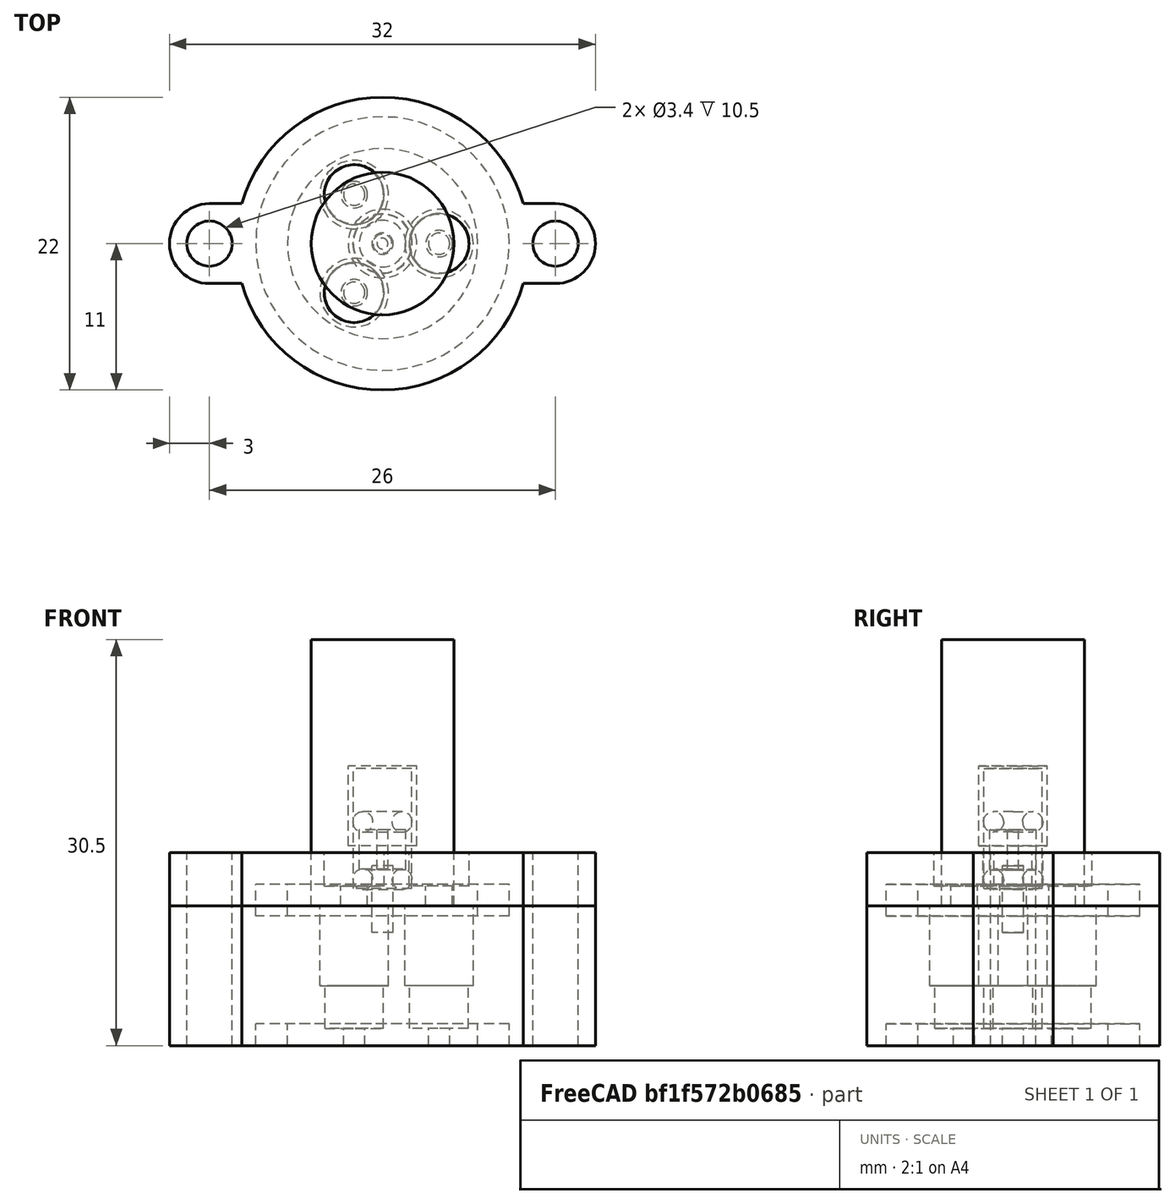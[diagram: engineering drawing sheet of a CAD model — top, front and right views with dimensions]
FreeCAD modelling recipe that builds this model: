
FCSTD DOCUMENT  (FreeCAD 0.17R13509 (Git))
Label: ceramic_wire_feedthroughs
License: All rights reserved
LicenseURL: http://en.wikipedia.org/wiki/All_rights_reserved
objects: Part::Cylinder×46, Part::MultiFuse×12, Part::Cut×9, Part::Box×8, Part::FeaturePython×4, Part::Feature×2, App::FeaturePython×1
note: 81 computed .brp shape members not serialized (recipe doc carries the construction recipe); baked Part::Feature solids carry a one-line shape summary decoded from their .brp

FEATURE [Part::Cylinder] Cylinder151  label="WireFeedsMount002"
  Angle = 360
  AttacherType = Attacher::AttachEngine3D
  Height = 11
  Placement = pos=(13,0,0) rot=(0,0,1;0rad)
  Radius = 1.7
FEATURE [Part::Cylinder] Cylinder155  label="Cylinder009"
  Angle = 360
  AttacherType = Attacher::AttachEngine3D
  Height = 2.38125
  Radius = 9.525
  expr: Radius = 3 / 4 * 25.399999999999999 / 2
  expr: Height = 3 / 32 * 25.399999999999999
FEATURE [Part::Cylinder] Cylinder154  label="Cylinder008"
  Angle = 360
  AttacherType = Attacher::AttachEngine3D
  Height = 2.38125
  Radius = 7.14375
  expr: Radius = 9 / 16 * 25.399999999999999 / 2
  expr: Height = 3 / 32 * 25.399999999999999
FEATURE [Part::Feature] Part__Feature001  label="TopOring"
  Placement = pos=(0,0,6.3) rot=(0,0,1;0rad)
  shape: bbox 4.839 x 4.839 x 1.524 mm, 4 faces (baked)
FEATURE [Part::Feature] Part__Feature002  label="BottomOring"
  Placement = pos=(0,0,2) rot=(0,0,1;0rad)
  shape: bbox 4.839 x 4.839 x 1.524 mm, 4 faces (baked)
FEATURE [Part::Cylinder] Cylinder153  label="Body"
  Angle = 360
  AttacherType = Attacher::AttachEngine3D
  Height = 4
  Radius = 11
FEATURE [Part::Cut] Cut019  label="Oring"
  Base = -> Cylinder155
  Placement = pos=(0,0,-0.75) rot=(0,0,1;0rad)
  Tool = -> Cylinder154
FEATURE [Part::Cylinder] Cylinder150  label="WireFeedsMount1"
  Angle = 360
  AttacherType = Attacher::AttachEngine3D
  Height = 11
  Placement = pos=(-13,0,0) rot=(0,0,1;0rad)
  Radius = 1.7
FEATURE [Part::Cylinder] Cylinder147  label="ThreadedSection"
  Angle = 360
  AttacherType = Attacher::AttachEngine3D
  Height = 1
  Placement = pos=(0,0,4.5) rot=(0,0,1;0rad)
  Radius = 1
FEATURE [Part::Cylinder] Cylinder149  label="FTBead"
  Angle = 360
  AttacherType = Attacher::AttachEngine3D
  Height = 3
  Placement = pos=(0,0,2.7) rot=(0,0,1;0rad)
  Radius = 1.75
  expr: Radius = 3.5 / 2
FEATURE [Part::Cylinder] Cylinder152  label="RFFeeds005"
  Angle = 360
  AttacherType = Attacher::AttachEngine3D
  Height = 20
  Radius = 5.35813
  expr: Placement.Base.x = 0
FEATURE [Part::Cylinder] Cylinder156  label="BottomWireOutlet"
  Angle = 360
  AttacherType = Attacher::AttachEngine3D
  Height = 5
  Placement = pos=(0,0,-2) rot=(0,0,1;0rad)
  Radius = 1
FEATURE [Part::Cylinder] Cylinder157  label="SealSubtraction"
  Angle = 360
  AttacherType = Attacher::AttachEngine3D
  Height = 8
  Placement = pos=(0,0,1.5) rot=(0,0,1;0rad)
  Radius = 2.25
FEATURE [Part::Cylinder] Cylinder  label="MountFlange1"
  Angle = 360
  AttacherType = Attacher::AttachEngine3D
  Height = 4
  Placement = pos=(-13,0,0) rot=(0,0,1;0rad)
  Radius = 3
FEATURE [Part::Box] Box  label="MountCube1"
  AttacherType = Attacher::AttachEngine3D
  Height = 4
  Length = 3
  Placement = pos=(-13,-3,0) rot=(0,0,1;0rad)
  Width = 6
FEATURE [Part::Box] Box001  label="MountCube002"
  AttacherType = Attacher::AttachEngine3D
  Height = 4
  Length = 3
  Placement = pos=(10,-3,0) rot=(0,0,1;0rad)
  Width = 6
FEATURE [Part::Cylinder] Cylinder158  label="MountFlange002"
  Angle = 360
  AttacherType = Attacher::AttachEngine3D
  Height = 4
  Placement = pos=(13,0,0) rot=(0,0,1;0rad)
  Radius = 3
FEATURE [Part::MultiFuse] Fusion
  Placement = pos=(4.25,0,0) rot=(0,0,1;0rad)
  Shapes = -> [Cylinder147,Cylinder157,Cylinder156]
FEATURE [Part::FeaturePython] Array  label="SealArray"  # Draft array (typed FeaturePython)
  Angle = 360
  ArrayType = 1
  Axis = (0,0,1)
  Base = -> Fusion
  Center = (0,0,0)
  Fuse = false
  IntervalAxis = (0,0,0)
  IntervalX = (1,0,0)
  IntervalY = (0,1,0)
  IntervalZ = (0,0,0)
  NumberPolar = 3
  NumberX = 2
  NumberY = 2
  NumberZ = 1
FEATURE [Part::Cylinder] Cylinder159  label="FTBeadHole"
  Angle = 360
  AttacherType = Attacher::AttachEngine3D
  Height = 17
  Radius = 0.405
  expr: Radius = 0.81000000000000005 / 2
FEATURE [Part::Cut] Cut020
  Base = -> Cylinder149
  Tool = -> Cylinder159
FEATURE [Part::Cylinder] Cylinder160  label="Cylinder010"
  Angle = 360
  AttacherType = Attacher::AttachEngine3D
  Height = 2.38125
  Radius = 9.525
  expr: Radius = 3 / 4 * 25.399999999999999 / 2
  expr: Height = 3 / 32 * 25.399999999999999
FEATURE [Part::Cylinder] Cylinder161  label="WireFeedsMount003"
  Angle = 360
  AttacherType = Attacher::AttachEngine3D
  Height = 11
  Placement = pos=(-13,0,0) rot=(0,0,1;0rad)
  Radius = 1.7
FEATURE [Part::Cylinder] Cylinder162  label="ThreadedSection001"
  Angle = 360
  AttacherType = Attacher::AttachEngine3D
  Height = 6
  Placement = pos=(0,0,4.5) rot=(0,0,1;0rad)
  Radius = 2.575
  expr: Radius = 5.1500000000000004 / 2
FEATURE [Part::Cylinder] Cylinder163  label="Cylinder011"
  Angle = 360
  AttacherType = Attacher::AttachEngine3D
  Height = 2.38125
  Radius = 7.14375
  expr: Radius = 9 / 16 * 25.399999999999999 / 2
  expr: Height = 3 / 32 * 25.399999999999999
FEATURE [Part::Cut] Cut022  label="Oring001"
  Base = -> Cylinder160
  Placement = pos=(0,0,-0.75) rot=(0,0,1;0rad)
  Tool = -> Cylinder163
FEATURE [Part::Cylinder] Cylinder164  label="Body001"
  Angle = 360
  AttacherType = Attacher::AttachEngine3D
  Height = 10.5
  Radius = 11
FEATURE [Part::Cylinder] Cylinder165  label="WireFeedsMount004"
  Angle = 360
  AttacherType = Attacher::AttachEngine3D
  Height = 11
  Placement = pos=(13,0,0) rot=(0,0,1;0rad)
  Radius = 1.7
FEATURE [Part::Cylinder] Cylinder166  label="BottomWireOutlet001"
  Angle = 360
  AttacherType = Attacher::AttachEngine3D
  Height = 5
  Placement = pos=(0,0,-2) rot=(0,0,1;0rad)
  Radius = 0.8
FEATURE [Part::Cylinder] Cylinder167  label="SealSubtraction001"
  Angle = 360
  AttacherType = Attacher::AttachEngine3D
  Height = 9
  Placement = pos=(0,0,1.3) rot=(0,0,1;0rad)
  Radius = 2.2
FEATURE [Part::Box] Box002  label="MountCube003"
  AttacherType = Attacher::AttachEngine3D
  Height = 10.5
  Length = 3
  Placement = pos=(10,-3,0) rot=(0,0,1;0rad)
  Width = 6
FEATURE [Part::Box] Box003  label="MountCube004"
  AttacherType = Attacher::AttachEngine3D
  Height = 10.5
  Length = 3
  Placement = pos=(-13,-3,0) rot=(0,0,1;0rad)
  Width = 6
FEATURE [Part::MultiFuse] Fusion004
  Placement = pos=(4.25,0,0) rot=(0,0,1;0rad)
  Shapes = -> [Cylinder162,Cylinder167,Cylinder166]
FEATURE [Part::Cylinder] Cylinder168  label="MountFlange003"
  Angle = 360
  AttacherType = Attacher::AttachEngine3D
  Height = 10.5
  Placement = pos=(-13,0,0) rot=(0,0,1;0rad)
  Radius = 3
FEATURE [Part::Cylinder] Cylinder169  label="MountFlange004"
  Angle = 360
  AttacherType = Attacher::AttachEngine3D
  Height = 10.5
  Placement = pos=(13,0,0) rot=(0,0,1;0rad)
  Radius = 3
FEATURE [Part::MultiFuse] Fusion003
  Shapes = -> [Cylinder169,Box002,Box003,Cylinder168,Cylinder164]
FEATURE [Part::FeaturePython] Array001  label="SealArray001"  # Draft array (typed FeaturePython)
  Angle = 360
  ArrayType = 1
  Axis = (0,0,1)
  Base = -> Fusion004
  Center = (0,0,0)
  Fuse = false
  IntervalAxis = (0,0,0)
  IntervalX = (1,0,0)
  IntervalY = (0,1,0)
  IntervalZ = (0,0,0)
  NumberPolar = 3
  NumberX = 2
  NumberY = 2
  NumberZ = 1
FEATURE [Part::MultiFuse] Fusion005
  Shapes = -> [Cylinder165,Cylinder161,Cut022,Array001]
FEATURE [Part::Cut] Cut021
  Base = -> Fusion003
  Placement = pos=(0,0,-10.5) rot=(0,0,1;0rad)
  Tool = -> Fusion005
FEATURE [Part::Cylinder] Cylinder170  label="Cylinder012"
  Angle = 360
  AttacherType = Attacher::AttachEngine3D
  Height = 2.38125
  Radius = 9.525
  expr: Radius = 3 / 4 * 25.399999999999999 / 2
  expr: Height = 3 / 32 * 25.399999999999999
FEATURE [Part::Cylinder] Cylinder171  label="WireFeedsMount005"
  Angle = 360
  AttacherType = Attacher::AttachEngine3D
  Height = 11
  Placement = pos=(-13,0,0) rot=(0,0,1;0rad)
  Radius = 1.7
FEATURE [Part::Cylinder] Cylinder172  label="ThreadedSection002"
  Angle = 360
  AttacherType = Attacher::AttachEngine3D
  Height = 6
  Placement = pos=(0,0,4.5) rot=(0,0,1;0rad)
  Radius = 2.575
  expr: Radius = 5.1500000000000004 / 2
FEATURE [Part::Cylinder] Cylinder173  label="Cylinder013"
  Angle = 360
  AttacherType = Attacher::AttachEngine3D
  Height = 2.38125
  Radius = 7.14375
  expr: Radius = 9 / 16 * 25.399999999999999 / 2
  expr: Height = 3 / 32 * 25.399999999999999
FEATURE [Part::Cut] Cut024  label="Oring002"
  Base = -> Cylinder170
  Placement = pos=(0,0,-0.75) rot=(0,0,1;0rad)
  Tool = -> Cylinder173
FEATURE [Part::Cylinder] Cylinder174  label="Body002"
  Angle = 360
  AttacherType = Attacher::AttachEngine3D
  Height = 10.5
  Radius = 11
FEATURE [Part::Cylinder] Cylinder175  label="WireFeedsMount006"
  Angle = 360
  AttacherType = Attacher::AttachEngine3D
  Height = 11
  Placement = pos=(13,0,0) rot=(0,0,1;0rad)
  Radius = 1.7
FEATURE [Part::Cylinder] Cylinder176  label="BottomWireOutlet002"
  Angle = 360
  AttacherType = Attacher::AttachEngine3D
  Height = 5
  Placement = pos=(0,0,-2) rot=(0,0,1;0rad)
  Radius = 0.8
FEATURE [Part::Cylinder] Cylinder177  label="SealSubtraction002"
  Angle = 360
  AttacherType = Attacher::AttachEngine3D
  Height = 9
  Placement = pos=(0,0,1.3) rot=(0,0,1;0rad)
  Radius = 2.2
FEATURE [Part::Box] Box004  label="MountCube005"
  AttacherType = Attacher::AttachEngine3D
  Height = 10.5
  Length = 3
  Placement = pos=(10,-3,0) rot=(0,0,1;0rad)
  Width = 6
FEATURE [App::FeaturePython] SetupSheet002  # Path/CAM operation (typed FeaturePython)
  ClearanceHeightExpression = StartDepth+SetupSheet.ClearanceHeightOffset
  ClearanceHeightOffset = 5
  FinalDepthExpression = OpFinalDepth
  HorizRapid = 0
  SafeHeightExpression = StartDepth+SetupSheet.SafeHeightOffset
  SafeHeightOffset = 3
  StartDepthExpression = OpStartDepth
  StepDownExpression = OpToolDiameter
  VertRapid = 0
FEATURE [Part::Box] Box005  label="MountCube006"
  AttacherType = Attacher::AttachEngine3D
  Height = 10.5
  Length = 3
  Placement = pos=(-13,-3,0) rot=(0,0,1;0rad)
  Width = 6
FEATURE [Part::MultiFuse] Fusion007
  Placement = pos=(4.25,0,0) rot=(0,0,1;0rad)
  Shapes = -> [Cylinder172,Cylinder177,Cylinder176]
FEATURE [Part::Cylinder] Cylinder178  label="MountFlange005"
  Angle = 360
  AttacherType = Attacher::AttachEngine3D
  Height = 10.5
  Placement = pos=(-13,0,0) rot=(0,0,1;0rad)
  Radius = 3
FEATURE [Part::Cylinder] Cylinder179  label="MountFlange006"
  Angle = 360
  AttacherType = Attacher::AttachEngine3D
  Height = 10.5
  Placement = pos=(13,0,0) rot=(0,0,1;0rad)
  Radius = 3
FEATURE [Part::MultiFuse] Fusion006
  Shapes = -> [Cylinder179,Box004,Box005,Cylinder178,Cylinder174]
FEATURE [Part::FeaturePython] Array002  label="SealArray002"  # Draft array (typed FeaturePython)
  Angle = 360
  ArrayType = 1
  Axis = (0,0,1)
  Base = -> Fusion007
  Center = (0,0,0)
  Fuse = false
  IntervalAxis = (0,0,0)
  IntervalX = (1,0,0)
  IntervalY = (0,1,0)
  IntervalZ = (0,0,0)
  NumberPolar = 3
  NumberX = 2
  NumberY = 2
  NumberZ = 1
FEATURE [Part::MultiFuse] Fusion008
  Shapes = -> [Cylinder175,Cylinder171,Cut024,Array002]
FEATURE [Part::Cut] Cut023
  Base = -> Fusion006
  Placement = pos=(0,0,-10.5) rot=(0,0,1;0rad)
  Tool = -> Fusion008
FEATURE [Part::Cylinder] Cylinder180  label="Cylinder014"
  Angle = 360
  AttacherType = Attacher::AttachEngine3D
  Height = 2.38125
  Radius = 7.14375
  expr: Radius = 9 / 16 * 25.399999999999999 / 2
  expr: Height = 3 / 32 * 25.399999999999999
FEATURE [Part::Cylinder] Cylinder181  label="MountFlange007"
  Angle = 360
  AttacherType = Attacher::AttachEngine3D
  Height = 10.5
  Placement = pos=(-13,0,0) rot=(0,0,1;0rad)
  Radius = 3
FEATURE [Part::Box] Box006  label="MountCube007"
  AttacherType = Attacher::AttachEngine3D
  Height = 10.5
  Length = 3
  Placement = pos=(-13,-3,0) rot=(0,0,1;0rad)
  Width = 6
FEATURE [Part::Cylinder] Cylinder182  label="WireFeedsMount007"
  Angle = 360
  AttacherType = Attacher::AttachEngine3D
  Height = 11
  Placement = pos=(13,0,0) rot=(0,0,1;0rad)
  Radius = 1.7
FEATURE [Part::Box] Box007  label="MountCube008"
  AttacherType = Attacher::AttachEngine3D
  Height = 10.5
  Length = 3
  Placement = pos=(10,-3,0) rot=(0,0,1;0rad)
  Width = 6
FEATURE [Part::Cylinder] Cylinder183  label="WireFeedsMount008"
  Angle = 360
  AttacherType = Attacher::AttachEngine3D
  Height = 11
  Placement = pos=(-13,0,0) rot=(0,0,1;0rad)
  Radius = 1.7
FEATURE [Part::Cylinder] Cylinder184  label="Body003"
  Angle = 360
  AttacherType = Attacher::AttachEngine3D
  Height = 10.5
  Radius = 11
FEATURE [Part::Cylinder] Cylinder185  label="MountFlange008"
  Angle = 360
  AttacherType = Attacher::AttachEngine3D
  Height = 10.5
  Placement = pos=(13,0,0) rot=(0,0,1;0rad)
  Radius = 3
FEATURE [Part::Cylinder] Cylinder186  label="BottomWireOutlet003"
  Angle = 360
  AttacherType = Attacher::AttachEngine3D
  Height = 5
  Placement = pos=(0,0,-2) rot=(0,0,1;0rad)
  Radius = 0.8
FEATURE [Part::MultiFuse] Fusion011
  Shapes = -> [Cylinder185,Box007,Box006,Cylinder181,Cylinder184]
FEATURE [Part::Cylinder] Cylinder187  label="ThreadedSection003"
  Angle = 360
  AttacherType = Attacher::AttachEngine3D
  Height = 6
  Placement = pos=(0,0,4.5) rot=(0,0,1;0rad)
  Radius = 2.575
  expr: Radius = 5.1500000000000004 / 2
FEATURE [Part::Cylinder] Cylinder188  label="Cylinder015"
  Angle = 360
  AttacherType = Attacher::AttachEngine3D
  Height = 2.38125
  Radius = 9.525
  expr: Radius = 3 / 4 * 25.399999999999999 / 2
  expr: Height = 3 / 32 * 25.399999999999999
FEATURE [Part::Cut] Cut025  label="Oring003"
  Base = -> Cylinder188
  Placement = pos=(0,0,-0.75) rot=(0,0,1;0rad)
  Tool = -> Cylinder180
FEATURE [Part::Cylinder] Cylinder189  label="SealSubtraction003"
  Angle = 360
  AttacherType = Attacher::AttachEngine3D
  Height = 9
  Placement = pos=(0,0,1.3) rot=(0,0,1;0rad)
  Radius = 2.2
FEATURE [Part::MultiFuse] Fusion009
  Placement = pos=(4.25,0,0) rot=(0,0,1;0rad)
  Shapes = -> [Cylinder187,Cylinder189,Cylinder186]
FEATURE [Part::FeaturePython] Array003  label="SealArray003"  # Draft array (typed FeaturePython)
  Angle = 360
  ArrayType = 1
  Axis = (0,0,1)
  Base = -> Fusion009
  Center = (0,0,0)
  Fuse = false
  IntervalAxis = (0,0,0)
  IntervalX = (1,0,0)
  IntervalY = (0,1,0)
  IntervalZ = (0,0,0)
  NumberPolar = 3
  NumberX = 2
  NumberY = 2
  NumberZ = 1
FEATURE [Part::MultiFuse] Fusion010
  Shapes = -> [Cylinder182,Cylinder183,Cut025,Array003]
FEATURE [Part::Cut] Cut026
  Base = -> Fusion011
  Placement = pos=(0,0,-10.5) rot=(0,0,1;0rad)
  Tool = -> Fusion010
FEATURE [Part::Cylinder] Cylinder192  label="ThreadedSection004"
  Angle = 360
  AttacherType = Attacher::AttachEngine3D
  Height = 6
  Placement = pos=(0,0,4.5) rot=(0,0,1;0rad)
  Radius = 2.575
  expr: Radius = 5.1500000000000004 / 2
FEATURE [Part::Cylinder] Cylinder196  label="BottomWireOutlet004"
  Angle = 360
  AttacherType = Attacher::AttachEngine3D
  Height = 5
  Placement = pos=(0,0,-2) rot=(0,0,1;0rad)
  Radius = 0.8
FEATURE [Part::Cylinder] Cylinder197  label="SealSubtraction004"
  Angle = 360
  AttacherType = Attacher::AttachEngine3D
  Height = 9
  Placement = pos=(0,0,1.3) rot=(0,0,1;0rad)
  Radius = 2.2
FEATURE [Part::MultiFuse] Fusion012
  Shapes = -> [Cylinder,Box,Cylinder153,Box001,Cylinder158]
FEATURE [Part::MultiFuse] Fusion013
  Shapes = -> [Array,Cylinder150,Cylinder151]
FEATURE [Part::Cut] Cut
  Base = -> Fusion012
  Tool = -> Fusion013
